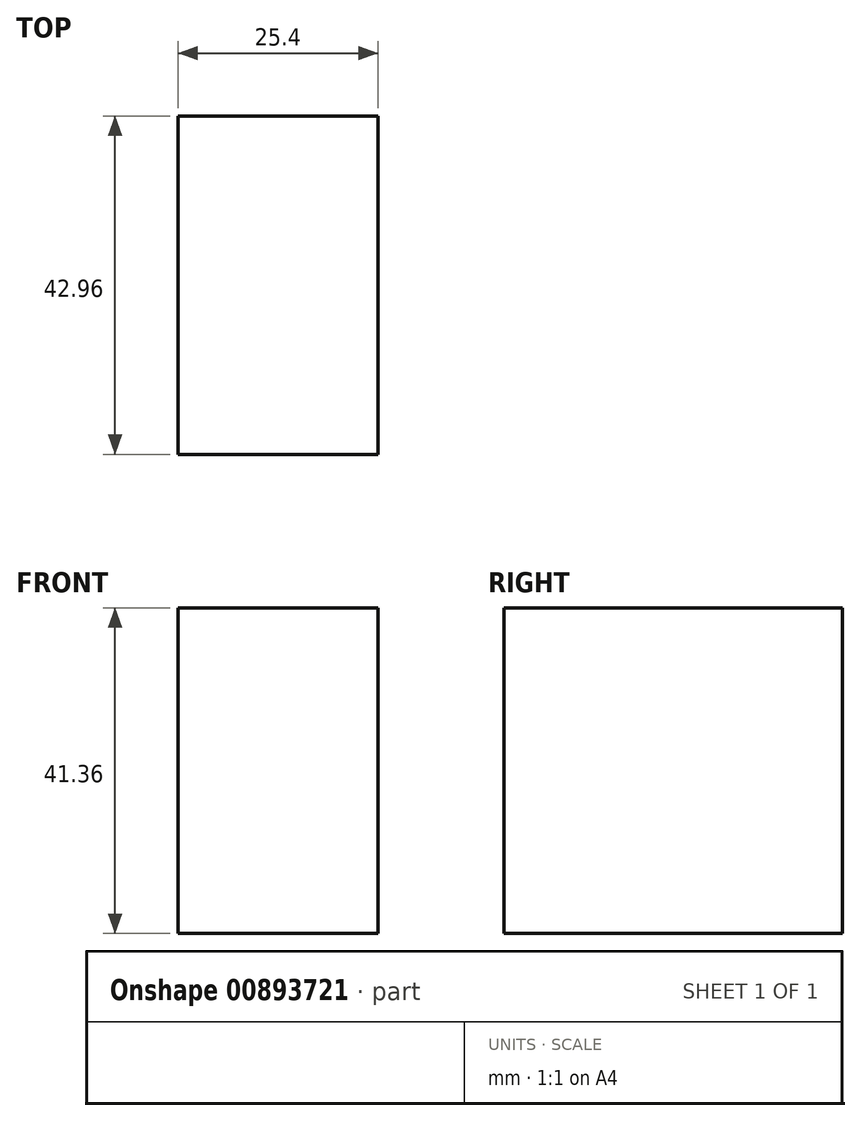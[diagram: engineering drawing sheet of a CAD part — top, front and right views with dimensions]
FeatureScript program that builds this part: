
annotation { "Feature Type Name" : "Feature", "Feature Type Description" : "" }
export const myFeature = defineFeature(function(context is Context, id is Id, definition is map)
    precondition{}
    {
        {
            var Q0;
            Q0=qCreatedBy(makeId("Right.planeOp"),FACE);
            var sketch = newSketch(context, id + "F0", { "sketchPlane" : qUnion([Q0])});
            skLineSegment(sketch, "E0.bottom", {"start": v(0, 0) * mm, "end": v(-42.96, 0) * mm});
            skLineSegment(sketch, "E0.top", {"start": v(0, 41.36) * mm, "end": v(-42.96, 41.36) * mm});
            skLineSegment(sketch, "E0.left", {"start": v(0, 0) * mm, "end": v(0, 41.36) * mm});
            skLineSegment(sketch, "E0.right", {"start": v(-42.96, 0) * mm, "end": v(-42.96, 41.36) * mm});
            skLineSegment(sketch, "E1", {"start": v(0, 15.71) * mm, "end": v(-7.3, 15.71) * mm});
            skLineSegment(sketch, "E2", {"start": v(0, 23.94) * mm, "end": v(-7.3, 23.94) * mm});
            skArc(sketch, "E3", {"start": v(-7.3, 23.94) * mm, "mid": v(-19.25, 19.83) * mm, "end": v(-7.3, 15.71) * mm});
            skSolve(sketch);
        }
        {
            var Q0;
            Q0 = qSketchRegion(id + "F0", true);
            extrude(context, id + "F1", {"entities" : qUnion([Q0]), "endBound" : BoundingType.SYMMETRIC, "depth" : 25.4 * mm, "offsetDistance" : 25.4 * mm});
        }
        {
            var Q0;
            Q0=sQuery(id+"F0.wireOp",EDGE,"E3");
            extrude(context, id + "F2", {"bodyType" : ToolBodyType.SURFACE, "surfaceEntities" : qUnion([Q0]), "depth" : 16.76 * mm, "offsetDistance" : 25.4 * mm});
        }
    });
